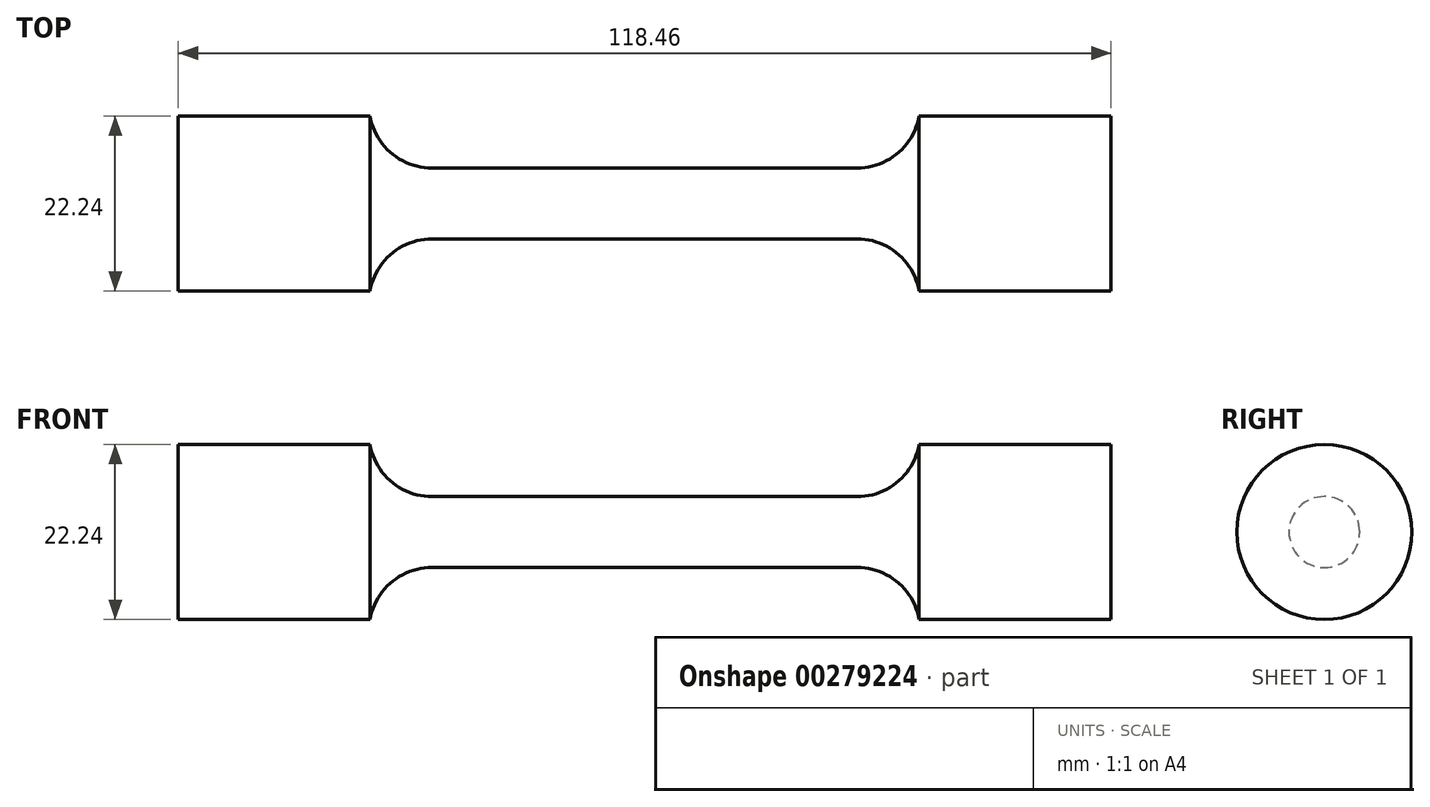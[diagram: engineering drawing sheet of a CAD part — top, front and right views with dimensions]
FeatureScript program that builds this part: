
annotation { "Feature Type Name" : "Feature", "Feature Type Description" : "" }
export const myFeature = defineFeature(function(context is Context, id is Id, definition is map)
    precondition{}
    {
        {
            var Q0;
            Q0=qCreatedBy(makeId("Front.planeOp"),FACE);
            var sketch = newSketch(context, id + "F0", { "sketchPlane" : qUnion([Q0])});
            skLineSegment(sketch, "E0", {"start": v(0, 4.5) * mm, "end": v(27, 4.5) * mm});
            skArc(sketch, "E1", {"start": v(27, 4.5) * mm, "mid": v(32.15, 6.37) * mm, "end": v(34.88, 11.12) * mm});
            skLineSegment(sketch, "E2", {"start": v(34.88, 11.12) * mm, "end": v(59.23, 11.12) * mm});
            skLineSegment(sketch, "E3", {"start": v(59.23, 11.12) * mm, "end": v(59.23, 0) * mm});
            skLineSegment(sketch, "E4.MirrorCS", {"start": v(0, 4.5) * mm, "end": v(-27, 4.5) * mm});
            skLineSegment(sketch, "E5.MirrorCS", {"start": v(-59.23, 11.12) * mm, "end": v(-59.23, 0) * mm});
            skLineSegment(sketch, "E6.MirrorCS", {"start": v(-34.88, 11.12) * mm, "end": v(-59.23, 11.12) * mm});
            skArc(sketch, "E7.MirrorCS", {"start": v(-27, 4.5) * mm, "mid": v(-32.15, 6.37) * mm, "end": v(-34.88, 11.12) * mm});
            skLineSegment(sketch, "E8", {"start": v(-59.23, 0) * mm, "end": v(59.23, 0) * mm});
            skSolve(sketch);
        }
        {
            var Q0;
            Q0=makeQuery(id+"F0.imprint","IMPRINT",FACE,{"disambiguationData":[TD([[makeQuery(id+"F0.imprint","IMPRINT",EDGE,{"derivedFrom":sQuery(id+"F0.wireOp",EDGE,"E0")}),-1.0]])]});
            var Q1;
            Q1=sQuery(id+"F0.wireOp",EDGE,"E8");
            revolve(context, id + "F1", {"entities" : qUnion([Q0]), "axis" : qUnion([Q1]), "revolveType" : RevolveType.FULL});
        }
    });
